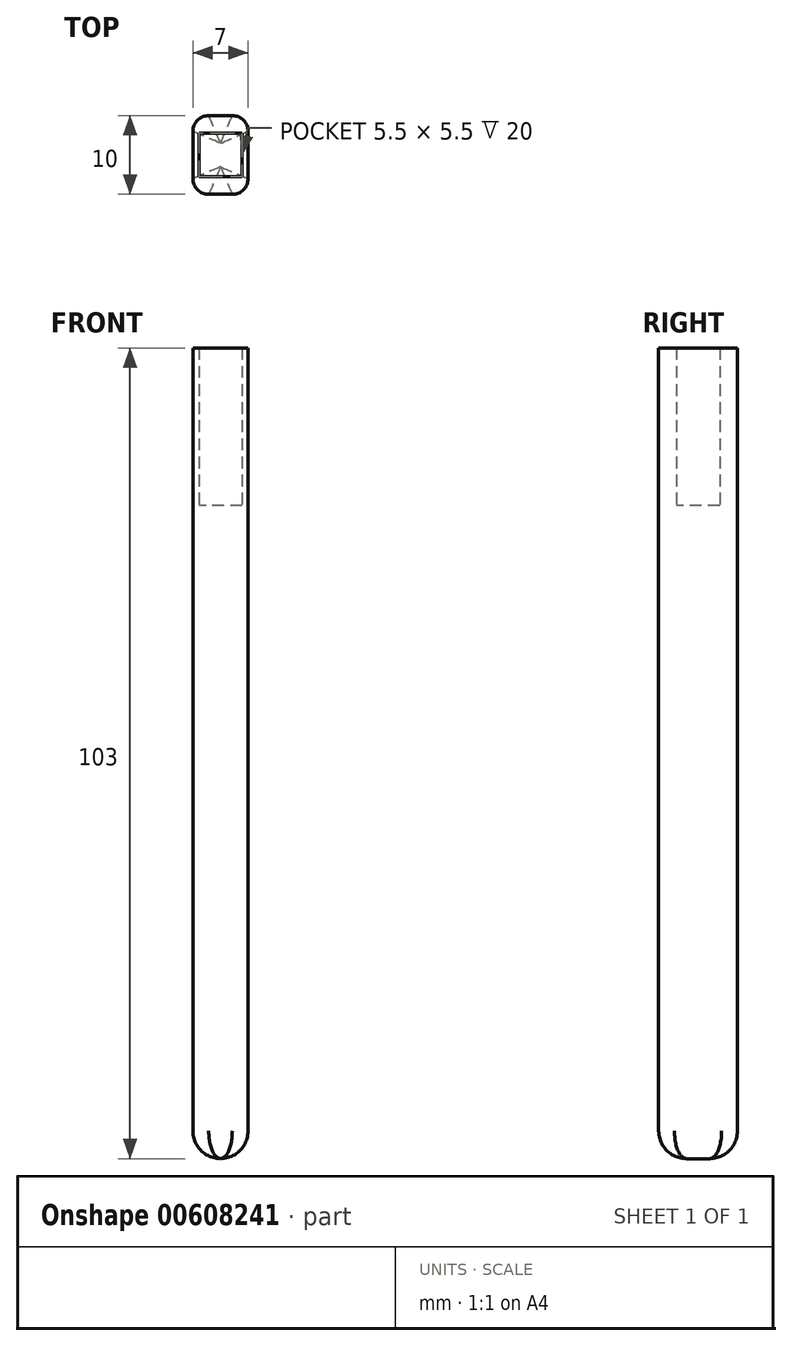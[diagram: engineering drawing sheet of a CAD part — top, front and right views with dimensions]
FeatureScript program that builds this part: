
annotation { "Feature Type Name" : "Feature", "Feature Type Description" : "" }
export const myFeature = defineFeature(function(context is Context, id is Id, definition is map)
    precondition{}
    {
        {
            var Q0;
            Q0=qCreatedBy(makeId("Top.planeOp"),FACE);
            var sketch = newSketch(context, id + "F0", { "sketchPlane" : qUnion([Q0])});
            skLineSegment(sketch, "E0.bottom", {"start": v(2.75, 2.75) * mm, "end": v(-2.75, 2.75) * mm});
            skLineSegment(sketch, "E0.top", {"start": v(2.75, -2.75) * mm, "end": v(-2.75, -2.75) * mm});
            skLineSegment(sketch, "E0.left", {"start": v(2.75, 2.75) * mm, "end": v(2.75, -2.75) * mm});
            skLineSegment(sketch, "E0.right", {"start": v(-2.75, 2.75) * mm, "end": v(-2.75, -2.75) * mm});
            skPoint(sketch, "E0.middle", {"position": v(0, 0) * mm});
            skLineSegment(sketch, "E1.bottom", {"start": v(3.5, 5) * mm, "end": v(-3.5, 5) * mm});
            skLineSegment(sketch, "E1.top", {"start": v(3.5, -5) * mm, "end": v(-3.5, -5) * mm});
            skLineSegment(sketch, "E1.left", {"start": v(3.5, 5) * mm, "end": v(3.5, -5) * mm});
            skLineSegment(sketch, "E1.right", {"start": v(-3.5, 5) * mm, "end": v(-3.5, -5) * mm});
            skSolve(sketch);
        }
        {
            var Q0;
            Q0=makeQuery(id+"F0.imprint","IMPRINT",FACE,{"disambiguationData":[TD([[makeQuery(id+"F0.imprint","IMPRINT",EDGE,{"derivedFrom":sQuery(id+"F0.wireOp",EDGE,"E0.bottom")}),-1.0]])]});
            extrude(context, id + "F1", {"entities" : qUnion([Q0]), "depth" : 20 * mm, "offsetDistance" : 25 * mm});
        }
        {
            var Q0;
            Q0=makeQuery(id+"F0.imprint","IMPRINT",FACE,{"disambiguationData":[TD([[makeQuery(id+"F0.imprint","IMPRINT",EDGE,{"derivedFrom":sQuery(id+"F0.wireOp",EDGE,"E0.bottom")}),1.0]])]});
            var Q1;
            Q1=makeQuery(id+"F0.imprint","IMPRINT",FACE,{"disambiguationData":[TD([[makeQuery(id+"F0.imprint","IMPRINT",EDGE,{"derivedFrom":sQuery(id+"F0.wireOp",EDGE,"E0.bottom")}),-1.0]])]});
            extrude(context, id + "F2", {"entities" : qUnion([Q0, Q1]), "operationType" : NewBodyOperationType.ADD, "oppositeDirection" : true, "depth" : 3 * mm, "offsetDistance" : 25 * mm});
        }
        {
            var Q0;
            Q0=makeQuery(id+"F2.opExtrude","CAP_FACE",FACE,{"disambiguationData":[OSD([sQuery(id+"F0.wireOp",EDGE,"E1.bottom"),sQuery(id+"F0.wireOp",EDGE,"E1.top"),sQuery(id+"F0.wireOp",EDGE,"E1.left"),sQuery(id+"F0.wireOp",EDGE,"E1.right")])],"isStart":false});
            extrude(context, id + "F3", {"entities" : qUnion([Q0]), "operationType" : NewBodyOperationType.ADD, "depth" : 80 * mm, "offsetDistance" : 25 * mm});
        }
        {
            var Q0;
            {var subQ0=sQuery(id+"F0.wireOp",EDGE,"E1.left");var subQ1=sQuery(id+"F0.wireOp",EDGE,"E1.bottom");Q0=makeQuery(id+"F3.boolean.opBoolean","MERGE",EDGE,{"derivedFrom":[makeQuery(id+"F2.boolean.opBoolean","MERGE",EDGE,{"derivedFrom":[makeQuery(id+"F1.opExtrude","SWEPT_EDGE",EDGE,{"disambiguationData":[OSD([subQ1,subQ0])]}),makeQuery(id+"F2.opExtrude","SWEPT_EDGE",EDGE,{"disambiguationData":[OSD([subQ1,subQ0])]})]}),makeQuery(id+"F3.opExtrude","SWEPT_EDGE",EDGE,{"disambiguationData":[OSD([subQ1,subQ0])]})]});}
            var Q1;
            {var subQ0=sQuery(id+"F0.wireOp",EDGE,"E1.right");var subQ1=sQuery(id+"F0.wireOp",EDGE,"E1.bottom");Q1=makeQuery(id+"F3.boolean.opBoolean","MERGE",EDGE,{"derivedFrom":[makeQuery(id+"F2.boolean.opBoolean","MERGE",EDGE,{"derivedFrom":[makeQuery(id+"F1.opExtrude","SWEPT_EDGE",EDGE,{"disambiguationData":[OSD([subQ1,subQ0])]}),makeQuery(id+"F2.opExtrude","SWEPT_EDGE",EDGE,{"disambiguationData":[OSD([subQ1,subQ0])]})]}),makeQuery(id+"F3.opExtrude","SWEPT_EDGE",EDGE,{"disambiguationData":[OSD([subQ1,subQ0])]})]});}
            var Q2;
            {var subQ0=sQuery(id+"F0.wireOp",EDGE,"E1.right");var subQ1=sQuery(id+"F0.wireOp",EDGE,"E1.top");Q2=makeQuery(id+"F3.boolean.opBoolean","MERGE",EDGE,{"derivedFrom":[makeQuery(id+"F2.boolean.opBoolean","MERGE",EDGE,{"derivedFrom":[makeQuery(id+"F1.opExtrude","SWEPT_EDGE",EDGE,{"disambiguationData":[OSD([subQ1,subQ0])]}),makeQuery(id+"F2.opExtrude","SWEPT_EDGE",EDGE,{"disambiguationData":[OSD([subQ1,subQ0])]})]}),makeQuery(id+"F3.opExtrude","SWEPT_EDGE",EDGE,{"disambiguationData":[OSD([subQ1,subQ0])]})]});}
            var Q3;
            {var subQ0=sQuery(id+"F0.wireOp",EDGE,"E1.left");var subQ1=sQuery(id+"F0.wireOp",EDGE,"E1.top");Q3=makeQuery(id+"F3.boolean.opBoolean","MERGE",EDGE,{"derivedFrom":[makeQuery(id+"F2.boolean.opBoolean","MERGE",EDGE,{"derivedFrom":[makeQuery(id+"F1.opExtrude","SWEPT_EDGE",EDGE,{"disambiguationData":[OSD([subQ1,subQ0])]}),makeQuery(id+"F2.opExtrude","SWEPT_EDGE",EDGE,{"disambiguationData":[OSD([subQ1,subQ0])]})]}),makeQuery(id+"F3.opExtrude","SWEPT_EDGE",EDGE,{"disambiguationData":[OSD([subQ1,subQ0])]})]});}
            fillet(context, id + "F4", {"entities" : qUnion([Q0, Q1, Q2, Q3]), "radius" : 2 * mm, "tangentPropagation" : true, "allowEdgeOverflow" : false});
        }
        {
            var Q0;
            Q0=makeQuery(id+"F3.opExtrude","CAP_FACE",FACE,{"disambiguationData":[OSD([sQuery(id+"F0.wireOp",EDGE,"E1.bottom"),sQuery(id+"F0.wireOp",EDGE,"E1.top"),sQuery(id+"F0.wireOp",EDGE,"E1.left"),sQuery(id+"F0.wireOp",EDGE,"E1.right")])],"isStart":false});
            fillet(context, id + "F5", {"entities" : qUnion([Q0]), "radius" : 3.5 * mm, "tangentPropagation" : true, "allowEdgeOverflow" : false});
        }
    });
